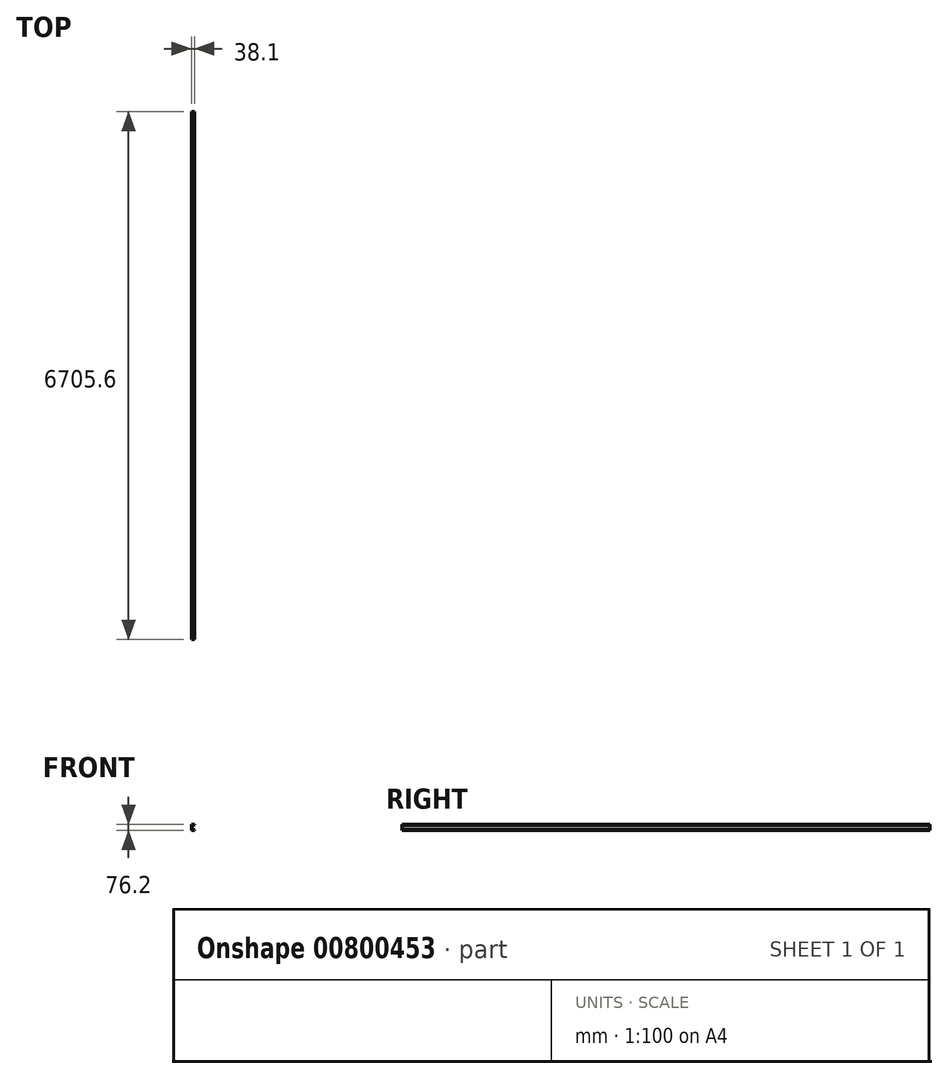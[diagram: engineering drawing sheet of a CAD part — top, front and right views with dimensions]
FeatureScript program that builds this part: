
annotation { "Feature Type Name" : "Feature", "Feature Type Description" : "" }
export const myFeature = defineFeature(function(context is Context, id is Id, definition is map)
    precondition{}
    {
        {
            var Q0;
            Q0=qCreatedBy(makeId("Front.planeOp"),FACE);
            var sketch = newSketch(context, id + "F0", { "sketchPlane" : qUnion([Q0])});
            skLineSegment(sketch, "E0", {"start": v(0, 0) * mm, "end": v(0, 76.2) * mm});
            skLineSegment(sketch, "E1", {"start": v(0, 76.2) * mm, "end": v(38.1, 76.2) * mm});
            skLineSegment(sketch, "E2", {"start": v(38.1, 76.2) * mm, "end": v(38.1, 71.12) * mm});
            skLineSegment(sketch, "E3", {"start": v(38.1, 71.12) * mm, "end": v(9.52, 60.72) * mm});
            skLineSegment(sketch, "E4", {"start": v(9.52, 60.72) * mm, "end": v(9.53, 15.48) * mm});
            skLineSegment(sketch, "E5", {"start": v(9.52, 15.48) * mm, "end": v(38.1, 5.08) * mm});
            skLineSegment(sketch, "E6", {"start": v(38.1, 5.08) * mm, "end": v(38.1, 0) * mm});
            skLineSegment(sketch, "E7", {"start": v(38.1, 0) * mm, "end": v(0, 0) * mm});
            skSolve(sketch);
        }
        {
            var Q0;
            Q0 = qSketchRegion(id + "F0", true);
            extrude(context, id + "F1", {"entities" : qUnion([Q0]), "depth" : 6705.6 * mm, "offsetDistance" : 25.4 * mm});
        }
    });
